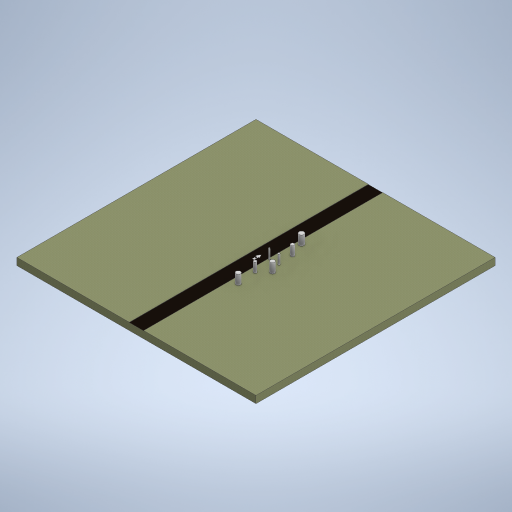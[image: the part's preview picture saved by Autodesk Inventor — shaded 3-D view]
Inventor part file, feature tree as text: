
AUTODESK INVENTOR PART (.ipt)
format: ipt  version: 2023 (Build 270158000, 158)  size: 315,392 bytes
history: native  units: in
note: dims shown in document units (in); Inventor stores cm internally (conversion verified against a paired STEP export)
features: extrude x6, sketch x6, pattern_linear x2, projected_geometry x1
ambient origin geometry x8: Origin, YZ Plane, XZ Plane, XY Plane, X Axis, Y Axis, Z Axis, Center Point
bodies: Solid1 (feature_tree)
feature tree (15):
  extrude  "Extrusion1"  Depth=3937.0079in
  extrude  "Extrusion2"  Depth=236.2205in
  extrude  "Extrusion3"  Depth=157.4803in
  pattern_linear  "Rectangular Pattern1"  Count1=50 Spacing1=0.0in
  pattern_linear  "Rectangular Pattern2"  Count1=2  [1 undecoded]
  extrude  "Extrusion4"  Depth=39.3701in
  extrude  "Extrusion5"  Depth=0.0394in TaperAngle=0.0deg
  extrude  "Extrusion6"  Depth=157.4803in TaperAngle=0.0deg
  sketch  "Sketch1"  dims[d0=3937.0079in d1=3937.0079in]
  sketch  "Sketch2"  dims[d2=118.1102in d3=0.0in d4=236.2205in]
  sketch  "Sketch3"  dims[d5=3.937in d6=0.0in d7=19.685in d8=19.685in d9=157.4803in d10=0.0in d11=0.7874in d13=472.4409in]
  projected_geometry  "Projected Loop1"
  sketch  "Sketch4"  dims[d14=0.7874in d16=472.4409in d17=39.3701in]
  sketch  "Sketch5"  dims[d18=157.4803in d19=0.0in d20=0.0394in d21=0.0in]
  sketch  "Sketch6"  dims[d23=19.685in d24=157.4803in d25=0.0in]
note: 1 required parameter value undecoded (feature->parameter linkage not recoverable at this tier; creation-order binding heuristic only, values carry confidence <= 0.55)
